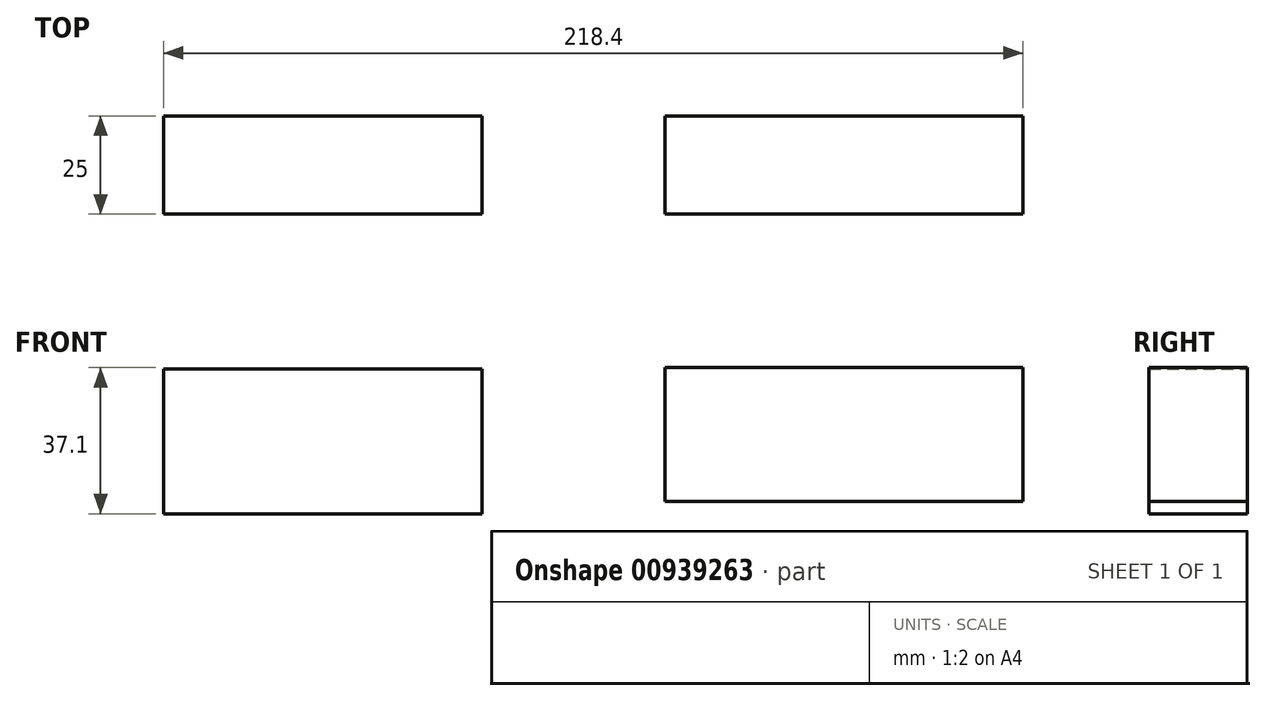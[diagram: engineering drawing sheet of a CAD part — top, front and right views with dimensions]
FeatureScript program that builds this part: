
annotation { "Feature Type Name" : "Feature", "Feature Type Description" : "" }
export const myFeature = defineFeature(function(context is Context, id is Id, definition is map)
    precondition{}
    {
        {
            var Q0;
            Q0=qCreatedBy(makeId("Front.planeOp"),FACE);
            var sketch = newSketch(context, id + "F0", { "sketchPlane" : qUnion([Q0])});
            skLineSegment(sketch, "E0.bottom", {"start": v(-127.47, 54.67) * mm, "end": v(-46.52, 54.67) * mm});
            skLineSegment(sketch, "E0.top", {"start": v(-127.47, 17.85) * mm, "end": v(-46.52, 17.85) * mm});
            skLineSegment(sketch, "E0.left", {"start": v(-127.47, 54.67) * mm, "end": v(-127.47, 17.85) * mm});
            skLineSegment(sketch, "E0.right", {"start": v(-46.52, 54.67) * mm, "end": v(-46.52, 17.85) * mm});
            skLineSegment(sketch, "E1.bottom", {"start": v(0, 54.95) * mm, "end": v(90.93, 54.95) * mm});
            skLineSegment(sketch, "E1.top", {"start": v(0, 20.94) * mm, "end": v(90.93, 20.94) * mm});
            skLineSegment(sketch, "E1.left", {"start": v(0, 54.95) * mm, "end": v(0, 20.94) * mm});
            skLineSegment(sketch, "E1.right", {"start": v(90.93, 54.95) * mm, "end": v(90.93, 20.94) * mm});
            skSolve(sketch);
        }
        {
            var Q0;
            Q0=makeQuery(id+"F0.imprint","IMPRINT",FACE,{"disambiguationData":[TD([[makeQuery(id+"F0.imprint","IMPRINT",EDGE,{"derivedFrom":sQuery(id+"F0.wireOp",EDGE,"E0.bottom")}),-1.0]])]});
            var Q1;
            Q1=makeQuery(id+"F0.imprint","IMPRINT",FACE,{"disambiguationData":[TD([[makeQuery(id+"F0.imprint","IMPRINT",EDGE,{"derivedFrom":sQuery(id+"F0.wireOp",EDGE,"E1.bottom")}),-1.0]])]});
            extrude(context, id + "F1", {"entities" : qUnion([Q0, Q1]), "depth" : 25 * mm, "offsetDistance" : 25 * mm});
        }
    });
